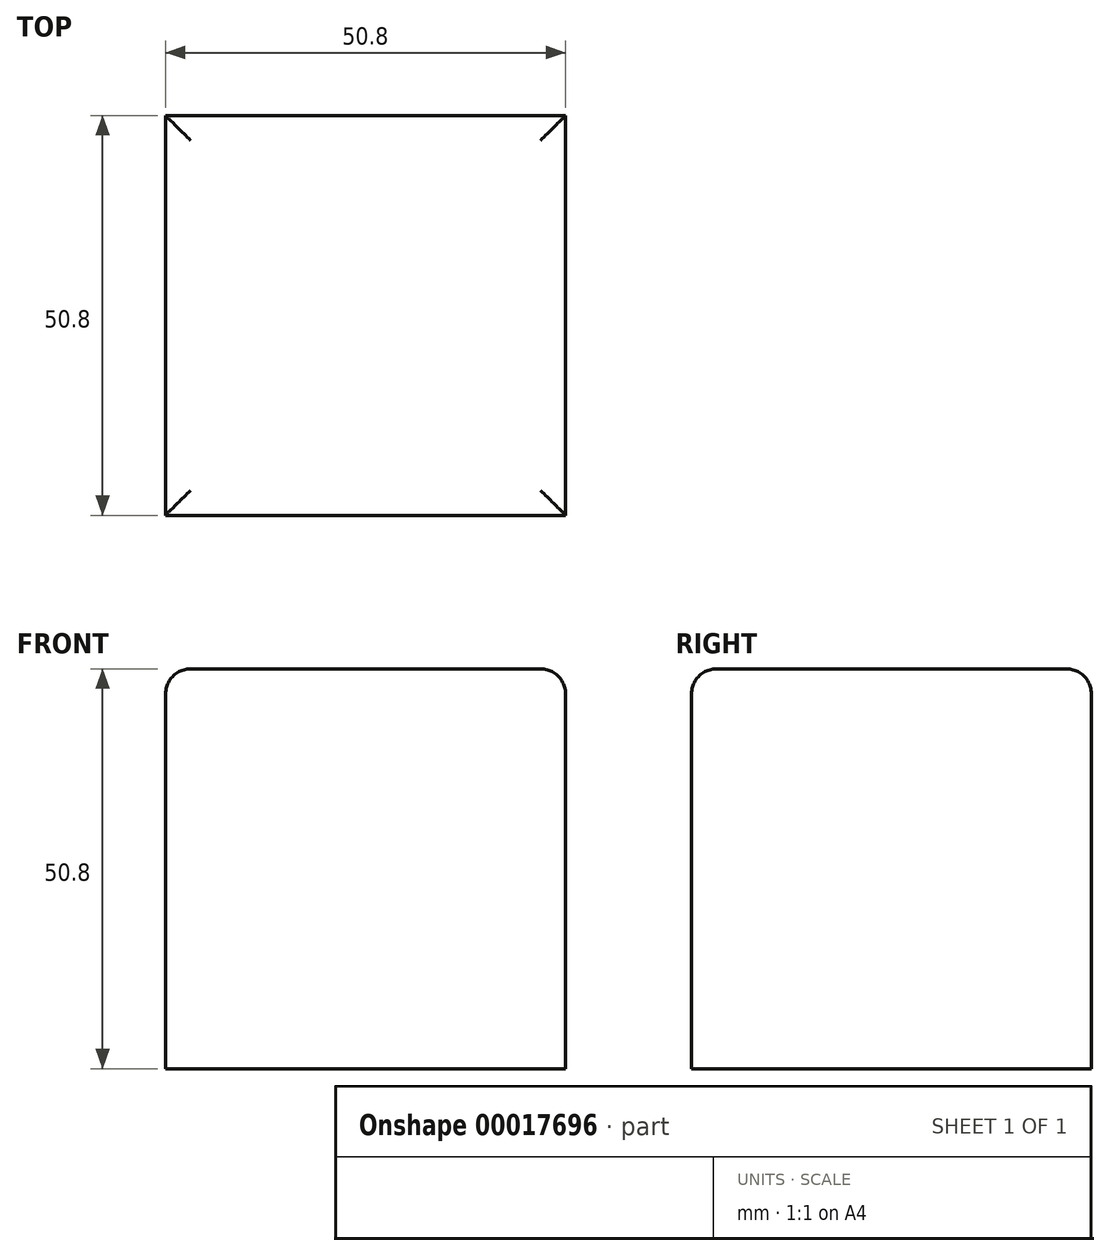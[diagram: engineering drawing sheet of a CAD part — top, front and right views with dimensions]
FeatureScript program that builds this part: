
annotation { "Feature Type Name" : "Feature", "Feature Type Description" : "" }
export const myFeature = defineFeature(function(context is Context, id is Id, definition is map)
    precondition{}
    {
        {
            var Q0;
            Q0=qCreatedBy(makeId("Front.planeOp"),FACE);
            var sketch = newSketch(context, id + "F0", { "sketchPlane" : qUnion([Q0])});
            skLineSegment(sketch, "E0.rect.bottom", {"start": v(25.4, 25.4) * mm, "end": v(-25.4, 25.4) * mm});
            skLineSegment(sketch, "E0.rect.top", {"start": v(25.4, -25.4) * mm, "end": v(-25.4, -25.4) * mm});
            skLineSegment(sketch, "E0.rect.left", {"start": v(25.4, 25.4) * mm, "end": v(25.4, -25.4) * mm});
            skLineSegment(sketch, "E0.rect.right", {"start": v(-25.4, 25.4) * mm, "end": v(-25.4, -25.4) * mm});
            skPoint(sketch, "E0.rect.middle", {"position": v(0, 0) * mm});
            skSolve(sketch);
        }
        {
            var Q0;
            Q0=makeQuery(id+"F0.imprint","IMPRINT",FACE,{"disambiguationData":[TD([[makeQuery(id+"F0.imprint","IMPRINT",EDGE,{"derivedFrom":sQuery(id+"F0.wireOp",EDGE,"E0.rect.bottom")}),1.0]])]});
            extrude(context, id + "F1", {"entities" : qUnion([Q0]), "endBound" : BoundingType.SYMMETRIC, "depth" : 50.8 * mm});
        }
        {
            var Q0;
            Q0=makeQuery(id+"F1.opExtrude","SWEPT_EDGE",EDGE,{"disambiguationData":[OSD([sQuery(id+"F0.wireOp",EDGE,"E0.rect.bottom"),sQuery(id+"F0.wireOp",EDGE,"E0.rect.right")])]});
            var Q1;
            Q1=makeQuery(id+"F1.opExtrude","CAP_EDGE",EDGE,{"disambiguationData":[OSD([sQuery(id+"F0.wireOp",EDGE,"E0.rect.bottom")])],"isStart":false});
            var Q2;
            Q2=makeQuery(id+"F1.opExtrude","SWEPT_EDGE",EDGE,{"disambiguationData":[OSD([sQuery(id+"F0.wireOp",EDGE,"E0.rect.bottom"),sQuery(id+"F0.wireOp",EDGE,"E0.rect.left")])]});
            var Q3;
            Q3=makeQuery(id+"F1.opExtrude","CAP_EDGE",EDGE,{"disambiguationData":[OSD([sQuery(id+"F0.wireOp",EDGE,"E0.rect.bottom")])],"isStart":true});
            fillet(context, id + "F2", {"entities" : qUnion([Q0, Q1, Q2, Q3]), "radius" : 3.17 * mm, "tangentPropagation" : true, "allowEdgeOverflow" : false});
        }
    });
